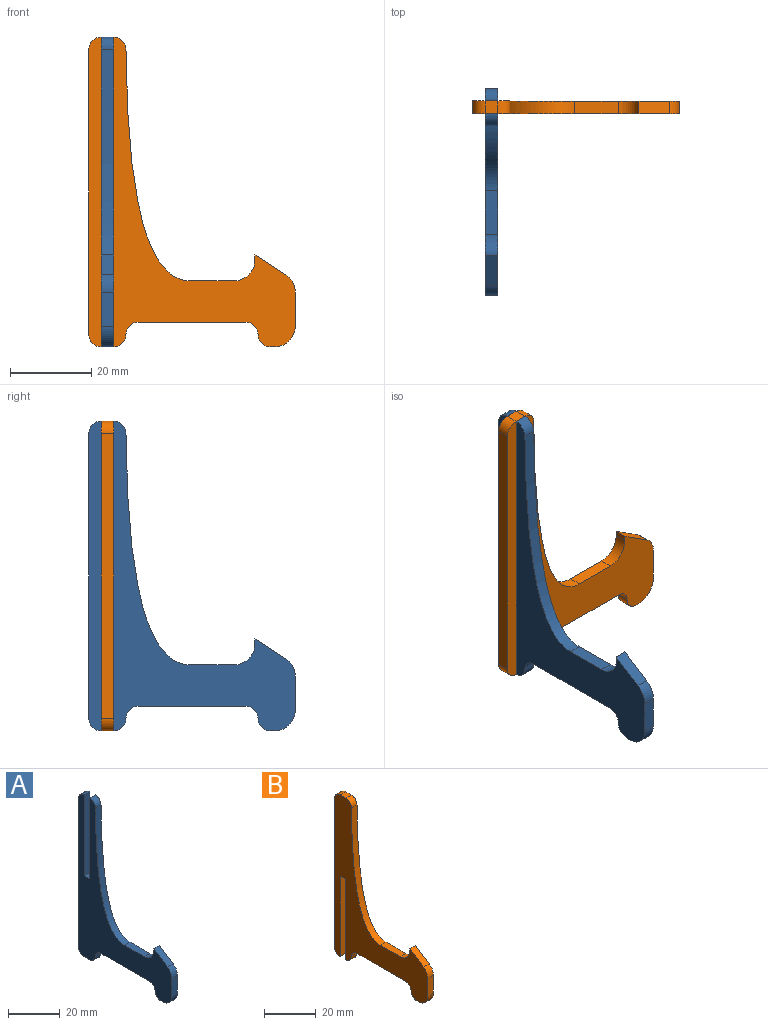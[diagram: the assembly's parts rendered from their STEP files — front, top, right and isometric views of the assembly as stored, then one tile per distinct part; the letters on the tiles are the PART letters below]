
ASSEMBLY  parts=2 mates=1
PART A: 25 faces, bbox 3x50.8x76.2 mm
  f0: plane 38.1x3.05mm, normal (0,1,0), area 116.1mm2, adj f1,f12,f13,f14
  f1: plane 3.05x0.01mm, normal (0,0,1), area 0mm2, adj f0,f13,f14,f15
  f2: extruded ~56.92x15.86mm, area 191.3mm2, adj f3,f13,f14,f15
  f3: plane 10.8x3.05mm, normal (0,0,1), area 32.9mm2, adj f2,f13,f14,f22
  f4: plane 3.05x1.27mm, normal (0,1,0), area 3.9mm2, adj f5,f13,f14,f22
  f5: plane 7.57x4.85mm, normal (0,-0.54,0.84), area 27.4mm2, adj f4,f13,f14,f23
  f6: plane 8.4x3.05mm, normal (0,-1,0), area 25.6mm2, adj f13,f14,f23,f24
  f7: plane 3.05x1.02mm, normal (0,0,-1), area 3.1mm2, adj f13,f14,f17,f24
  f8: plane 26.42x3.05mm, normal (0,0,-1), area 80.5mm2, adj f13,f14,f16,f19
  f9: plane 3.05x3.05mm, normal (0,0,-1), area 9.3mm2, adj f13,f14,f18,f20
  f10: plane 70.1x3.05mm, normal (0,1,0), area 213.7mm2, adj f13,f14,f20,f21
  f11: plane 38.1x3.05mm, normal (0,-1,0), area 116.1mm2, adj f12,f13,f14,f21
  f12: plane 3.05x3.05mm, normal (0,0,1), area 9.3mm2, adj f0,f11,f13,f14
  f13: plane 76.2x50.8mm, normal (1,0,0), area 1242.5mm2, adj f0,f1,f2,f3,f4,f5,f6,f7
  f14: plane 76.2x50.8mm, normal (-1,0,0), area 1242.5mm2, adj f0,f1,f2,f3,f4,f5,f6,f7
  f15: cylinder r=3.05mm len=3.05mm, axis (-1,0,0), area 14.5mm2, adj f1,f2,f13,f14
  f16: cylinder r=3.05mm len=3.05mm, axis (1,0,0), area 14.6mm2, adj f8,f13,f14,f17
  f17: cylinder r=3.05mm len=3.05mm, axis (-1,0,0), area 14.6mm2, adj f7,f13,f14,f16
  f18: cylinder r=3.05mm len=3.05mm, axis (-1,0,0), area 14.6mm2, adj f9,f13,f14,f19
  f19: cylinder r=3.05mm len=3.05mm, axis (1,0,0), area 14.6mm2, adj f8,f13,f14,f18
  f20: cylinder r=3.05mm len=3.05mm, axis (1,0,0), area 14.6mm2, adj f9,f10,f13,f14
  f21: cylinder r=3.05mm len=3.05mm, axis (-1,0,0), area 14.6mm2, adj f10,f11,f13,f14
  f22: cylinder r=5.08mm len=5.08mm, axis (1,0,0), area 24.3mm2, adj f3,f4,f13,f14
  f23: cylinder r=5.08mm len=4.28mm, axis (-1,0,0), area 15.5mm2, adj f5,f6,f13,f14
  f24: cylinder r=5.08mm len=5.08mm, axis (-1,0,0), area 24.3mm2, adj f6,f7,f13,f14
PART B: 24 faces, bbox 3x50.8x76.2 mm
  f0: extruded ~56.92x15.86mm, area 191.3mm2, adj f1,f12,f13,f20
  f1: plane 10.8x3.05mm, normal (0,0,1), area 32.9mm2, adj f0,f12,f13,f21
  f2: plane 3.05x1.27mm, normal (0,1,0), area 3.9mm2, adj f3,f12,f13,f21
  f3: plane 7.57x4.85mm, normal (0,-0.54,0.84), area 27.4mm2, adj f2,f12,f13,f22
  f4: plane 8.4x3.05mm, normal (0,-1,0), area 25.6mm2, adj f12,f13,f22,f23
  f5: plane 3.05x1.02mm, normal (0,0,-1), area 3.1mm2, adj f12,f13,f15,f23
  f6: plane 26.42x3.05mm, normal (0,0,-1), area 80.5mm2, adj f12,f13,f14,f17
  f7: plane 38.1x3.05mm, normal (0,1,0), area 116.1mm2, adj f8,f12,f13,f16
  f8: plane 3.05x3.05mm, normal (0,0,-1), area 9.3mm2, adj f7,f9,f12,f13
  f9: plane 38.1x3.05mm, normal (0,-1,0), area 116.1mm2, adj f8,f12,f13,f18
  f10: plane 70.1x3.05mm, normal (0,1,0), area 213.7mm2, adj f12,f13,f18,f19
  f11: plane 3.06x3.05mm, normal (0,0,1), area 9.3mm2, adj f12,f13,f19,f20
  f12: plane 76.2x50.8mm, normal (1,0,0), area 1242.5mm2, adj f0,f1,f2,f3,f4,f5,f6,f7
  f13: plane 76.2x50.8mm, normal (-1,0,0), area 1242.5mm2, adj f0,f1,f2,f3,f4,f5,f6,f7
  f14: cylinder r=3.05mm len=3.05mm, axis (1,0,0), area 14.6mm2, adj f6,f12,f13,f15
  f15: cylinder r=3.05mm len=3.05mm, axis (-1,0,0), area 14.6mm2, adj f5,f12,f13,f14
  f16: cylinder r=3.05mm len=3.05mm, axis (-1,0,0), area 14.6mm2, adj f7,f12,f13,f17
  f17: cylinder r=3.05mm len=3.05mm, axis (1,0,0), area 14.6mm2, adj f6,f12,f13,f16
  f18: cylinder r=3.05mm len=3.05mm, axis (1,0,0), area 14.6mm2, adj f9,f10,f12,f13
  f19: cylinder r=3.05mm len=3.05mm, axis (-1,0,0), area 14.6mm2, adj f10,f11,f12,f13
  f20: cylinder r=3.05mm len=3.05mm, axis (-1,0,0), area 14.5mm2, adj f0,f11,f12,f13
  f21: cylinder r=5.08mm len=5.08mm, axis (1,0,0), area 24.3mm2, adj f1,f2,f12,f13
  f22: cylinder r=5.08mm len=4.28mm, axis (-1,0,0), area 15.5mm2, adj f3,f4,f12,f13
  f23: cylinder r=5.08mm len=5.08mm, axis (-1,0,0), area 24.3mm2, adj f4,f5,f12,f13
PLACE A at identity
PLACE B rot(axis=(0,0,1),90deg) t=(22.35,19.3,0)mm
MATE planar B.f8 <-> A.f12  axis (0,0,-1) through (1.52,20.83,0)mm
